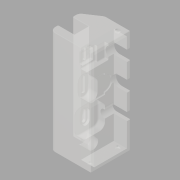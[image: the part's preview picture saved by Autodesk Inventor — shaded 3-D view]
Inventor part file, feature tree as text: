
AUTODESK INVENTOR PART (.ipt)
format: ipt  version: 2019 (Build 230136000, 136)  size: 1,064,448 bytes
history: native  units: mm
features: extrude x9, sketch x9, thicken_offset x6, other x5, fillet x3, projected_geometry x3, plane x2, boolean_combine x2, hole x2, mirror x2, chamfer x1
ambient origin geometry x8: Origin, YZ Plane, XZ Plane, XY Plane, X Axis, Y Axis, Z Axis, Center Point
bodies: Solid1 (feature_tree), Solid2 (feature_tree), Solid3 (feature_tree), Solid4 (feature_tree), Solid5 (feature_tree), Solid6 (feature_tree)
feature tree (44):
  other  "Monitor with Plugs.iam"
  other  "MageDok Screen.ipt:1"
  other  "USB C Right Angle Plug.ipt:1"
  other  "HDMI Mini Right Angle Plug.ipt:1"
  other  "USB Micro Right Angle Plug.ipt:1"
  plane  "Work Plane1"
  extrude  "Extrusion1"  Depth=2.54mm
  thicken_offset  "Thicken1"
  thicken_offset  "Thicken2"
  thicken_offset  "Thicken3"
  boolean_combine  "Combine1"
  extrude  "Extrusion2"  Depth=2.54mm
  boolean_combine  "Combine2"
  thicken_offset  "Thicken4"
  extrude  "Extrusion3"  Depth=0.25mm
  extrude  "Extrusion4"  Depth=0.25mm
  sketch  "Sketch5"  dims[d9=0.25mm d10=0.25mm]
  extrude  "Extrusion5"  Depth=0.25mm
  extrude  "Extrusion6"  Depth=2.54mm
  extrude  "Extrusion7"  Depth=0.15mm
  extrude  "Extrusion8"  Depth=0.15mm TaperAngle=0.0deg
  thicken_offset  "Thicken5"
  thicken_offset  "Thicken6"
  chamfer  "Chamfer1"  Distance=10.0mm
  fillet  "Fillet1"  Radius=10.0mm
  fillet  "Fillet2"  Radius=6.5mm
  fillet  "Fillet3"  Radius=8.5mm
  extrude  "Extrusion9"  Depth=10.0mm TaperAngle=0.0deg
  hole  "Hole1"  [1 undecoded]
  plane  "Work Plane2"
  mirror  "Mirror1"
  hole  "Hole2"  [1 undecoded]
  mirror  "Mirror2"
  sketch  "Sketch1"  dims[d0=10.0mm d1=2.54mm]
  sketch  "Sketch2"  dims[d2=10.0mm d3=2.54mm]
  projected_geometry  "Projected Loop1"
  sketch  "Sketch3"  dims[d4=30.0mm d5=0.0mm d6=0.25mm]
  sketch  "Sketch4"  dims[d7=0.25mm d8=0.25mm]
  projected_geometry  "Projected Loop2"
  sketch  "Sketch6"  dims[d11=0.25mm d12=2.54mm]
  projected_geometry  "Projected Loop3"
  sketch  "Sketch7"  dims[d13=10.0mm d14=0.0mm d15=0.15mm]
  sketch  "Sketch8"  dims[d16=0.15mm d17=3.25mm d18=0.0mm]
  sketch  "Sketch9"  dims[d19=2.54mm d20=10.0mm d21=0.0mm d22=10.0mm d23=0.0mm d24=6.5mm d25=0.0mm d26=8.5mm d27=0.0mm d28=12.7mm d29=0.0mm d30=8.0mm d31=12.0mm d32=45.0deg d33=4.0mm d34=1.0mm d35=0.5mm d36=0.15mm d37=0.15mm d38=0.15mm d39=0.15mm d40=1.321mm d41=0.25mm d42=4.0mm d43=2.0mm d44=90.0deg d45=4.0mm d46=20.594885mm d47=1.321mm d48=1.0mm d49=3.0mm d50=1.15mm d51=90.0deg d52=5.5mm d53=0.0mm d54=0.125mm d55=2.5mm d56=1.5mm d57=10.0mm d58=0.0mm]
note: 2 required parameter values undecoded (feature->parameter linkage not recoverable at this tier; creation-order binding heuristic only, values carry confidence <= 0.55)
